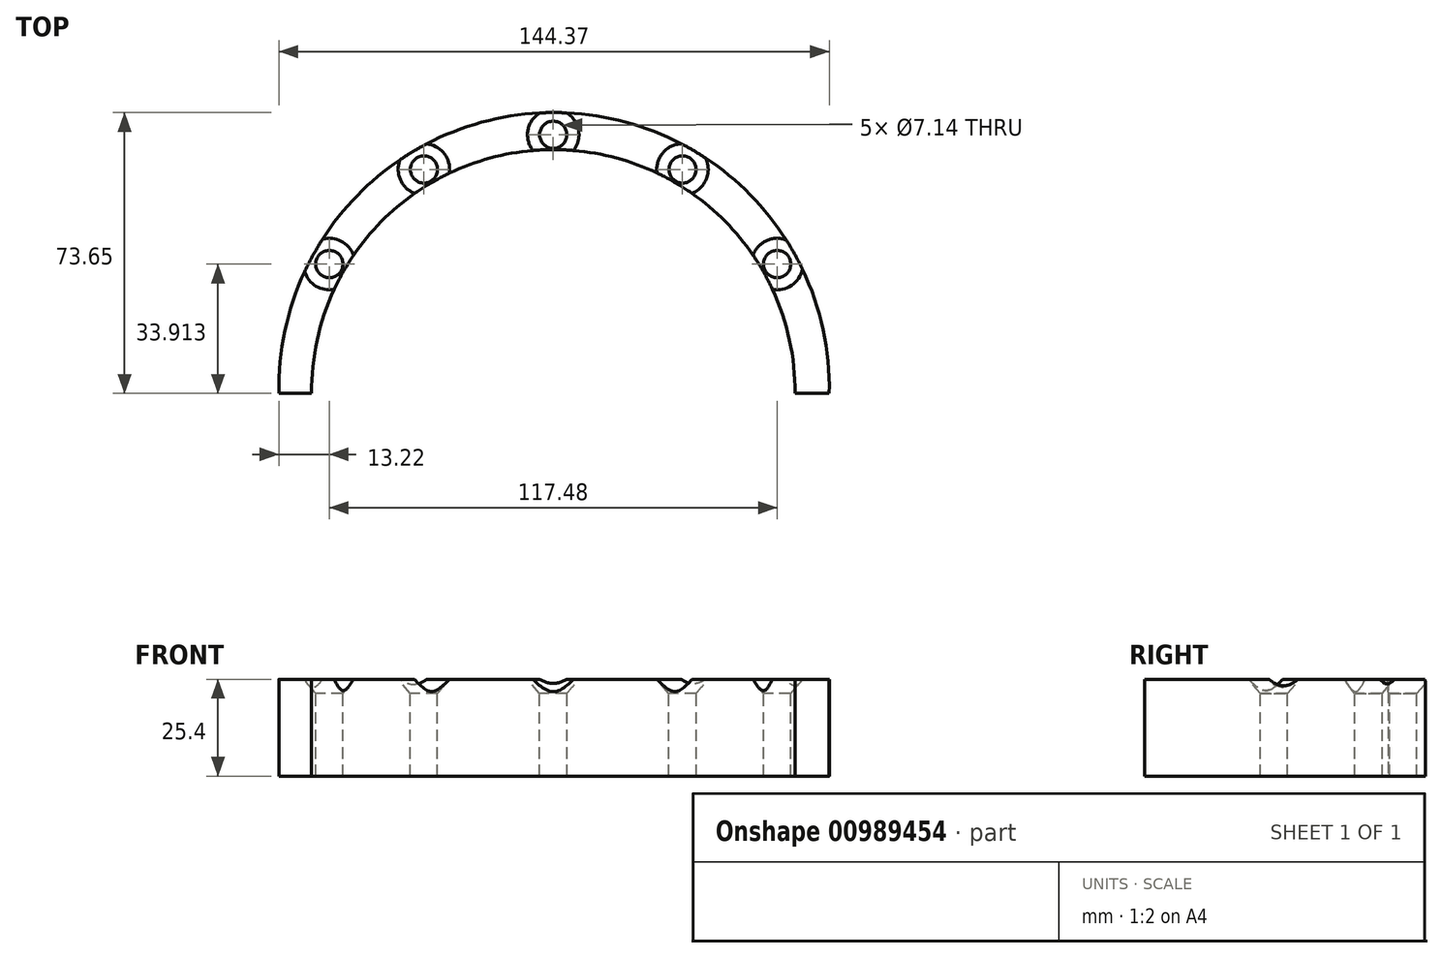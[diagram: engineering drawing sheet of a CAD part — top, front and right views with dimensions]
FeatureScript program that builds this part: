
annotation { "Feature Type Name" : "Feature", "Feature Type Description" : "" }
export const myFeature = defineFeature(function(context is Context, id is Id, definition is map)
    precondition{}
    {
        {
            var Q0;
            Q0=qCreatedBy(makeId("Top.planeOp"),FACE);
            var sketch = newSketch(context, id + "F0", { "sketchPlane" : qUnion([Q0])});
            skArc(sketch, "E0", {"start": v(72.4, 0) * mm, "mid": v(0.23, 73.65) * mm, "end": v(-71.94, 0) * mm});
            skLineSegment(sketch, "E1", {"start": v(-71.94, 0) * mm, "end": v(-63.38, 0) * mm});
            skLineSegment(sketch, "E2", {"start": v(72.4, 0) * mm, "end": v(63.42, 0) * mm});
            skArc(sketch, "E3", {"start": v(63.42, 0) * mm, "mid": v(0.02, 63.93) * mm, "end": v(-63.38, 0) * mm});
            skSolve(sketch);
        }
        {
            var Q0;
            Q0=makeQuery(id+"F0.imprint","IMPRINT",FACE,{"disambiguationData":[TD([[makeQuery(id+"F0.imprint","IMPRINT",EDGE,{"derivedFrom":sQuery(id+"F0.wireOp",EDGE,"E0")}),1.0]])]});
            extrude(context, id + "F1", {"entities" : qUnion([Q0]), "depth" : 25.4 * mm, "offsetDistance" : 25.4 * mm});
        }
        {
            var Q0;
            Q0=makeQuery(id+"F1.opExtrude","CAP_FACE",FACE,{"disambiguationData":[OSD([sQuery(id+"F0.wireOp",EDGE,"E0"),sQuery(id+"F0.wireOp",EDGE,"E1"),sQuery(id+"F0.wireOp",EDGE,"E2"),sQuery(id+"F0.wireOp",EDGE,"E3")])],"isStart":false});
            var sketch = newSketch(context, id + "F2", { "sketchPlane" : qUnion([Q0])});
            skCircle(sketch, "E4", {"center": v(-67.66, 0.26) * mm, "radius": 4.29 * mm});
            skPoint(sketch, "E4.first.point", {"position": v(-71.94, 0) * mm});
            skPoint(sketch, "E4.second.point", {"position": v(-63.38, 0) * mm});
            skPoint(sketch, "E4.third.point", {"position": v(-67.66, 4.55) * mm});
            skPoint(sketch, "E4.third.point.positionSnap0", {"position": v(-67.66, 0) * mm});
            skSolve(sketch);
        }
        {
            var Q0;
            {var subQ5=makeQuery(id+"F1.opExtrude","CAP_EDGE",EDGE,{"disambiguationData":[OSD([sQuery(id+"F0.wireOp",EDGE,"E2")])],"isStart":false});Q0=makeQuery(id+"F2.imprint","IMPRINT",FACE,{"disambiguationData":[TD([[makeQuery(id+"F2.imprint","IMPRINT",EDGE,{"derivedFrom":subQ5}),-1.0]])]});}
            var sketch = newSketch(context, id + "F3", { "sketchPlane" : qUnion([Q0])});
            skPoint(sketch, "E5", {"position": v(-67.83, 0) * mm});
            skPoint(sketch, "E6.1.0", {"position": v(-58.74, 33.91) * mm});
            skPoint(sketch, "E6.2.0", {"position": v(-33.91, 58.74) * mm});
            skPoint(sketch, "E6.3.0", {"position": v(0, 67.83) * mm});
            skPoint(sketch, "E6.4.0", {"position": v(33.91, 58.74) * mm});
            skPoint(sketch, "E6.5.0", {"position": v(58.74, 33.91) * mm});
            skPoint(sketch, "E6.6.0", {"position": v(67.83, 0) * mm});
            skPoint(sketch, "E6.center", {"position": v(0, 0) * mm});
            skLineSegment(sketch, "E6.anchor1", {"start": v(0, 0) * mm, "end": v(-67.83, 0) * mm, "construction": true});
            skLineSegment(sketch, "E6.anchor2", {"start": v(0, 0) * mm, "end": v(67.83, 0) * mm, "construction": true});
            skSolve(sketch);
        }
        {
            var Q0;
            Q0=sQuery(id+"F3.wireOp",VERTEX,"E6.1.0");
            var Q1;
            Q1=sQuery(id+"F3.wireOp",VERTEX,"E6.2.0");
            var Q2;
            Q2=sQuery(id+"F3.wireOp",VERTEX,"E6.3.0");
            var Q3;
            Q3=sQuery(id+"F3.wireOp",VERTEX,"E6.4.0");
            var Q4;
            Q4=sQuery(id+"F3.wireOp",VERTEX,"E6.5.0");
            var Q5;
            Q5=makeQuery(id+"F1.opExtrude","SWEPT_BODY",BODY,{"disambiguationData":[OSD([sQuery(id+"F0.wireOp",EDGE,"E0"),sQuery(id+"F0.wireOp",EDGE,"E1"),sQuery(id+"F0.wireOp",EDGE,"E2"),sQuery(id+"F0.wireOp",EDGE,"E3")])]});
            hole(context, id + "F4", {"style" : HoleStyle.C_SINK, "endStyle" : HoleEndStyle.THROUGH, "standardTappedOrClearance" : lookupTablePath({ "fit" : "Normal (ASME)", "standard" : "ANSI", "size" : "1/4", "type" : "Clearance" }), "standardBlindInLast" : lookupTablePath({ "fit" : "Normal", "standard" : "ANSI", "engagement" : "75%", "pitch" : "20 tpi", "size" : "1/4", "type" : "Clearance & tapped" }), "holeDiameter" : 7.14 * mm, "cSinkDiameter" : 13.5 * mm, "cSinkAngle" : 82 * degree, "majorDiameter" : 6.35 * mm, "isTappedThrough" : true, "tappedDepth" : 12.7 * mm, "tapClearance" : 3, "locations" : qUnion([Q0, Q1, Q2, Q3, Q4]), "scope" : qUnion([Q5])});
        }
    });
